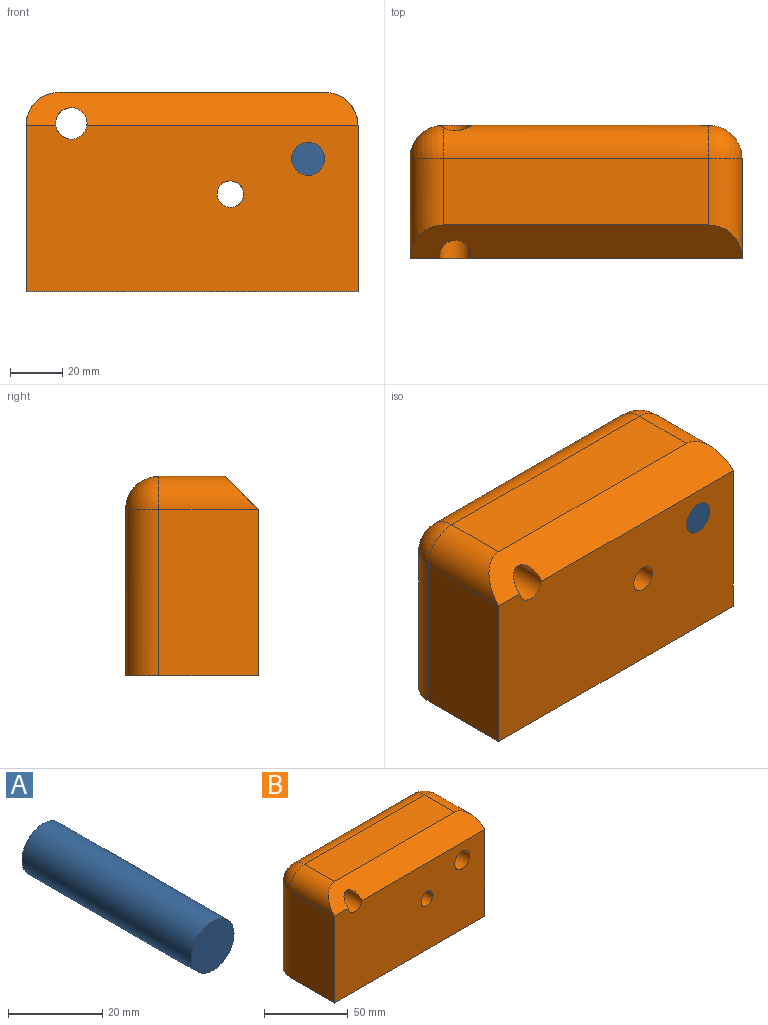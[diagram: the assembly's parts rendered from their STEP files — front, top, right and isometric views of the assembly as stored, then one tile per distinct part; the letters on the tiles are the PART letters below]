
ASSEMBLY  parts=2 mates=1
PART A: 3 faces, bbox 12.7x50.8x12.7 mm
  f0: cylinder r=6.35mm len=50.8mm, axis (0,1,0), area 2026.8mm2, adj f1,f2
  f1: plane 12.7x12.7mm, normal (0,-1,0), area 126.7mm2, adj f0
  f2: plane 12.7x12.7mm, normal (0,1,0), area 126.7mm2, adj f0
PART B: 17 faces, bbox 127x50.8x76.2 mm
  f0: plane 63.5x38.1mm, normal (-1,0,0), area 2419.3mm2, adj f1,f6,f14,f16
  f1: plane 127x50.8mm, normal (0,0,-1), area 6382.4mm2, adj f0,f2,f6,f7,f13,f16
  f2: plane 63.5x38.1mm, normal (1,0,0), area 2419.3mm2, adj f1,f6,f11,f13
  f3: cylinder r=6.35mm len=50.8mm, axis (0,1,0), area 2026.8mm2, adj f6,f7
  f4: cylinder r=6.01mm len=50.8mm, axis (0,1,0), area 1808.6mm2, adj f6,f7,f9,f10,f15,f16
  f5: plane 101.6x25.4mm, normal (0,0,1), area 2580.6mm2, adj f9,f10,f11,f14
  f6: plane 127x63.5mm, normal (0,-1,0), area 7810.4mm2, adj f0,f1,f2,f3,f4,f8,f9
  f7: plane 101.6x63.5mm, normal (0,1,0), area 6199.9mm2, adj f1,f3,f4,f8,f10,f13,f16
  f8: cylinder r=5.07mm len=50.8mm, axis (0,-1,0), area 1619.2mm2, adj f6,f7
  f9: plane 127x12.7mm, normal (0,-0.71,0.71), area 2088.6mm2, adj f4,f5,f6,f11,f14
  f10: cylinder r=12.7mm len=101.6mm, axis (-1,0,0), area 1961.9mm2, adj f4,f5,f7,f12,f15
  f11: cylinder r=12.7mm len=38.1mm, axis (0,1,0), area 598.8mm2, adj f2,f5,f9,f12
  f12: sphere r=12.7mm, area 253.4mm2, adj f10,f11,f13
  f13: cylinder r=12.7mm len=63.5mm, axis (0,0,1), area 1266.8mm2, adj f1,f2,f7,f12
  f14: cylinder r=12.7mm len=38.1mm, axis (0,-1,0), area 598.8mm2, adj f0,f5,f9,f15
  f15: sphere r=12.7mm, area 248.6mm2, adj f4,f10,f14,f16
  f16: cylinder r=12.7mm len=63.5mm, axis (0,0,-1), area 1264.4mm2, adj f0,f1,f4,f7,f15
PLACE A t=(48.43,14.75,-3.17)mm
PLACE B t=(-25.07,14.75,-28.84)mm fixed
MATE cylindrical A.f0 <-> B.f3  axis (0,1,0) through (4.69,14.75,31.16)mm
